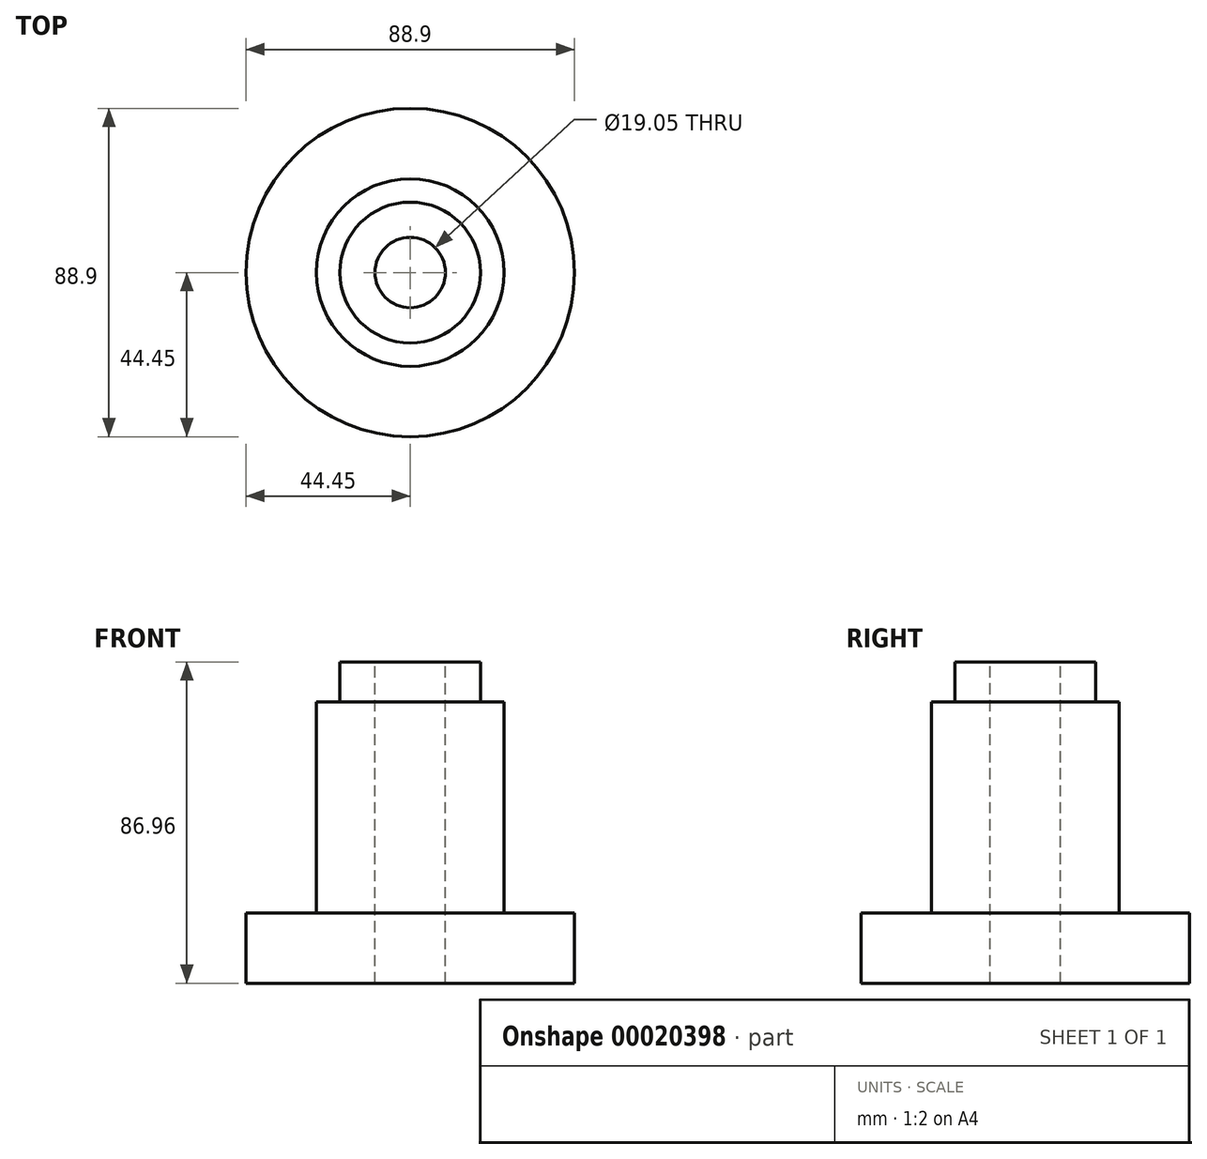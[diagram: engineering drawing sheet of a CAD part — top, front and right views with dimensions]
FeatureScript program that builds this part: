
annotation { "Feature Type Name" : "Feature", "Feature Type Description" : "" }
export const myFeature = defineFeature(function(context is Context, id is Id, definition is map)
    precondition{}
    {
        {
            var Q0;
            Q0=qCreatedBy(makeId("Front.planeOp"),FACE);
            var sketch = newSketch(context, id + "F0", { "sketchPlane" : qUnion([Q0])});
            skLineSegment(sketch, "E0.rect.bottom", {"start": v(-44.45, 9.52) * mm, "end": v(-25.4, 9.52) * mm});
            skLineSegment(sketch, "E0.rect.top", {"start": v(-44.45, -9.52) * mm, "end": v(0, -9.52) * mm});
            skLineSegment(sketch, "E0.rect.left", {"start": v(-44.45, 9.52) * mm, "end": v(-44.45, -9.52) * mm});
            skPoint(sketch, "E0.rect.middle", {"position": v(0, 0) * mm});
            skLineSegment(sketch, "E1.top", {"start": v(-25.4, 66.67) * mm, "end": v(-19.05, 66.67) * mm});
            skLineSegment(sketch, "E1.left", {"start": v(-25.4, 9.52) * mm, "end": v(-25.4, 66.67) * mm});
            skPoint(sketch, "E2.end.orphan", {"position": v(-25.4, 0) * mm});
            skPoint(sketch, "E2.start.orphan", {"position": v(-44.45, 0) * mm});
            skPoint(sketch, "E3.orphan", {"position": v(0, -9.52) * mm});
            skPoint(sketch, "E4.start.orphan", {"position": v(0, 9.52) * mm});
            skLineSegment(sketch, "E5.top", {"start": v(-19.05, 77.43) * mm, "end": v(0, 77.43) * mm});
            skLineSegment(sketch, "E5.left", {"start": v(-19.05, 66.67) * mm, "end": v(-19.05, 77.43) * mm});
            skPoint(sketch, "E6.start.orphan", {"position": v(-25.4, 38.1) * mm});
            skLineSegment(sketch, "E7", {"start": v(0, 77.43) * mm, "end": v(0, -9.52) * mm});
            skPoint(sketch, "E8.orphan", {"position": v(44.45, -9.52) * mm});
            skSolve(sketch);
        }
        {
            var Q0;
            Q0=makeQuery(id+"F0.imprint","IMPRINT",FACE,{"disambiguationData":[TD([[makeQuery(id+"F0.imprint","IMPRINT",EDGE,{"derivedFrom":sQuery(id+"F0.wireOp",EDGE,"E0.rect.bottom")}),-1.0]])]});
            var Q1;
            Q1=sQuery(id+"F0.wireOp",EDGE,"E7");
            revolve(context, id + "F1", {"entities" : qUnion([Q0]), "axis" : qUnion([Q1]), "revolveType" : RevolveType.ONE_DIRECTION, "oppositeDirection" : true, "angle" : 360 * degree});
        }
        {
            var Q0;
            Q0=makeQuery(id+"F1.opRevolve","SWEPT_FACE",FACE,{"disambiguationData":[OSD([sQuery(id+"F0.wireOp",EDGE,"E5.top")])]});
            var sketch = newSketch(context, id + "F2", { "sketchPlane" : qUnion([Q0])});
            skCircle(sketch, "E9", {"center": v(0, 0) * mm, "radius": 9.53 * mm});
            skSolve(sketch);
        }
        {
            var Q0;
            Q0=makeQuery(id+"F2.imprint","IMPRINT",FACE,{"disambiguationData":[TD([[makeQuery(id+"F2.imprint","IMPRINT",EDGE,{"derivedFrom":sQuery(id+"F2.wireOp",EDGE,"E9")}),1.0]])]});
            extrude(context, id + "F3", {"entities" : qUnion([Q0]), "operationType" : NewBodyOperationType.REMOVE, "endBound" : BoundingType.THROUGH_ALL, "oppositeDirection" : true, "depth" : 25.4 * mm});
        }
    });
